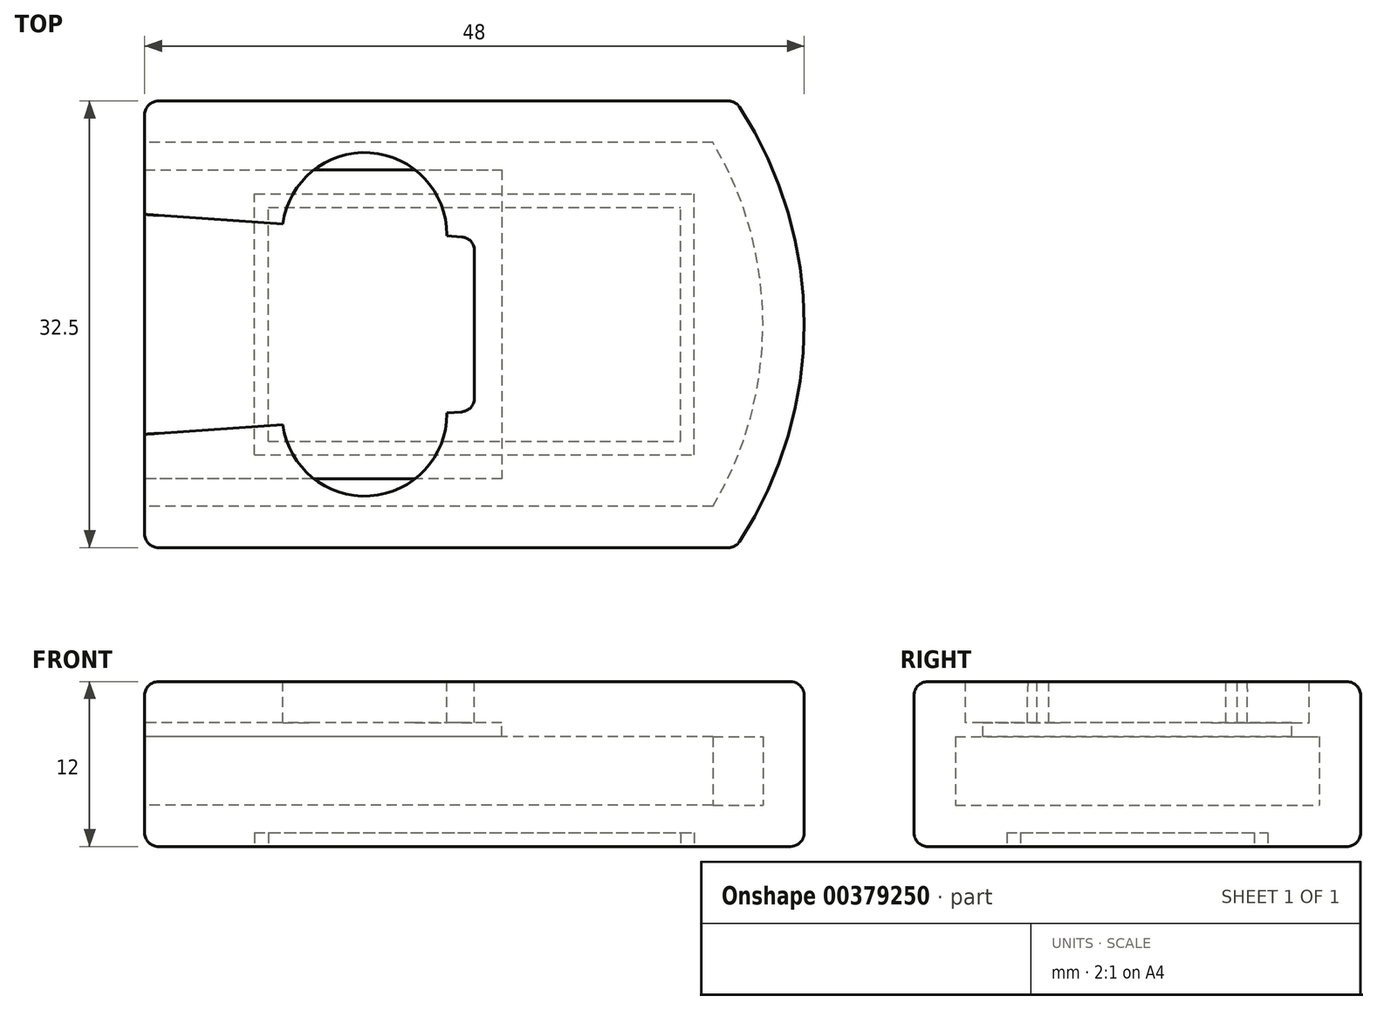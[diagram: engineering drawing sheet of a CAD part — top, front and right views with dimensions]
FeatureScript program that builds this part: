
annotation { "Feature Type Name" : "Feature", "Feature Type Description" : "" }
export const myFeature = defineFeature(function(context is Context, id is Id, definition is map)
    precondition{}
    {
        {
            var Q0;
            Q0=qCreatedBy(makeId("Top.planeOp"),FACE);
            var sketch = newSketch(context, id + "F0", { "sketchPlane" : qUnion([Q0])});
            skLineSegment(sketch, "E0.bottom", {"start": v(24, -16.25) * mm, "end": v(-24, -16.25) * mm});
            skLineSegment(sketch, "E0.top", {"start": v(24, 16.25) * mm, "end": v(-24, 16.25) * mm});
            skLineSegment(sketch, "E0.left", {"start": v(24, -16.25) * mm, "end": v(24, 16.25) * mm});
            skLineSegment(sketch, "E0.right", {"start": v(-24, -16.25) * mm, "end": v(-24, 16.25) * mm});
            skPoint(sketch, "E0.middle", {"position": v(0, 0) * mm});
            skArc(sketch, "E1", {"start": v(19, -16.25) * mm, "mid": v(24, 0) * mm, "end": v(19, 16.25) * mm});
            skSolve(sketch);
        }
        {
            var Q0;
            {var subQ4=sQuery(id+"F0.wireOp",EDGE,"E0.right");Q0=makeQuery(id+"F0.imprint","IMPRINT",FACE,{"disambiguationData":[TD([[makeQuery(id+"F0.imprint","IMPRINT",EDGE,{"derivedFrom":subQ4}),-1.0]])]});}
            extrude(context, id + "F1", {"entities" : qUnion([Q0]), "depth" : 12 * mm});
        }
        {
            var Q0;
            Q0=makeQuery(id+"F1.opExtrude","SWEPT_FACE",FACE,{"disambiguationData":[OSD([sQuery(id+"F0.wireOp",EDGE,"E0.right")])]});
            shell(context, id + "F2", {"entities" : qUnion([Q0]), "thickness" : 3 * mm});
        }
        {
            var Q0;
            Q0=makeQuery(id+"F1.opExtrude","CAP_FACE",FACE,{"disambiguationData":[OSD([sQuery(id+"F0.wireOp",EDGE,"E0.bottom"),sQuery(id+"F0.wireOp",EDGE,"E0.top"),sQuery(id+"F0.wireOp",EDGE,"E0.right"),sQuery(id+"F0.wireOp",EDGE,"FjGHQm9p-3ohD-EudD-jZ4d-5vYzKEwLbSdo")])],"isStart":false});
            var sketch = newSketch(context, id + "F3", { "sketchPlane" : qUnion([Q0])});
            skLineSegment(sketch, "E2.0.0", {"start": v(-24, -16.25) * mm, "end": v(-24, -16.25) * mm});
            skLineSegment(sketch, "E2.0.2", {"start": v(24, 16.25) * mm, "end": v(-24, 16.25) * mm});
            skLineSegment(sketch, "E2.0.3", {"start": v(-24, 16.25) * mm, "end": v(-24, -16.25) * mm});
            skLineSegment(sketch, "E3.bottom", {"start": v(-8, 12.5) * mm, "end": v(-8, 12.5) * mm});
            skLineSegment(sketch, "E3.top", {"start": v(-8, -12.5) * mm, "end": v(-8, -12.5) * mm});
            skLineSegment(sketch, "E3.left", {"start": v(-14, 6.5) * mm, "end": v(-14, -6.5) * mm});
            skLineSegment(sketch, "E3.right", {"start": v(-2, 6.5) * mm, "end": v(-2, -6.5) * mm});
            skPoint(sketch, "E3.middle", {"position": v(-8, 0) * mm});
            skLineSegment(sketch, "E4", {"start": v(-24, 0) * mm, "end": v(24, 0) * mm, "construction": true});
            skPoint(sketch, "E5.visualSharp", {"position": v(-14, 12.5) * mm});
            skArc(sketch, "E5.filletArc", {"start": v(-8, 12.5) * mm, "mid": v(-12.24, 10.74) * mm, "end": v(-14, 6.5) * mm});
            skPoint(sketch, "E6.visualSharp", {"position": v(-2, 12.5) * mm});
            skArc(sketch, "E6.filletArc", {"start": v(-2, 6.5) * mm, "mid": v(-3.76, 10.74) * mm, "end": v(-8, 12.5) * mm});
            skPoint(sketch, "E7.visualSharp", {"position": v(-2, -12.5) * mm});
            skArc(sketch, "E7.filletArc", {"start": v(-8, -12.5) * mm, "mid": v(-3.76, -10.74) * mm, "end": v(-2, -6.5) * mm});
            skPoint(sketch, "E8.visualSharp", {"position": v(-14, -12.5) * mm});
            skArc(sketch, "E8.filletArc", {"start": v(-14, -6.5) * mm, "mid": v(-12.24, -10.74) * mm, "end": v(-8, -12.5) * mm});
            skLineSegment(sketch, "E9", {"start": v(-24, 8) * mm, "end": v(0, 6.3) * mm});
            skLineSegment(sketch, "E10", {"start": v(0, 6.3) * mm, "end": v(0, 0) * mm});
            skLineSegment(sketch, "E11.MirrorCS", {"start": v(-24, -8) * mm, "end": v(0, -6.3) * mm});
            skLineSegment(sketch, "E12.MirrorCS", {"start": v(0, -6.3) * mm, "end": v(0, 0) * mm});
            skSolve(sketch);
        }
        {
            var Q0;
            {var subQ0=sQuery(id+"F3.wireOp",EDGE,"E5.filletArc");Q0=makeQuery(id+"F3.imprint","IMPRINT",FACE,{"disambiguationData":[TD([[makeQuery(id+"F3.imprint","IMPRINT",EDGE,{"derivedFrom":subQ0}),1.0]])]});}
            var Q1;
            {var subQ0=sQuery(id+"F3.wireOp",EDGE,"E7.filletArc");Q1=makeQuery(id+"F3.imprint","IMPRINT",FACE,{"disambiguationData":[TD([[makeQuery(id+"F3.imprint","IMPRINT",EDGE,{"derivedFrom":subQ0}),1.0]])]});}
            var Q2;
            {var subQ1=sQuery(id+"F3.wireOp",EDGE,"E3.left");Q2=makeQuery(id+"F3.imprint","IMPRINT",FACE,{"disambiguationData":[TD([[makeQuery(id+"F3.imprint","IMPRINT",EDGE,{"derivedFrom":subQ1}),1.0]])]});}
            var Q3;
            {var subQ1=sQuery(id+"F3.wireOp",EDGE,"E3.left");Q3=makeQuery(id+"F3.imprint","IMPRINT",FACE,{"disambiguationData":[TD([[makeQuery(id+"F3.imprint","IMPRINT",EDGE,{"derivedFrom":subQ1}),-1.0]])]});}
            var Q4;
            {var subQ4=sQuery(id+"F3.wireOp",EDGE,"E10");Q4=makeQuery(id+"F3.imprint","IMPRINT",FACE,{"disambiguationData":[TD([[makeQuery(id+"F3.imprint","IMPRINT",EDGE,{"derivedFrom":subQ4}),-1.0]])]});}
            var Q5;
            {var subQ0=sQuery(id+"F0.wireOp",EDGE,"FjGHQm9p-3ohD-EudD-jZ4d-5vYzKEwLbSdo");var subQ1=sQuery(id+"F0.wireOp",EDGE,"E0.right");var subQ2=sQuery(id+"F0.wireOp",EDGE,"E0.top");var subQ3=sQuery(id+"F0.wireOp",EDGE,"E0.bottom");Q5=makeQuery(id+"F2.opShell","OFFSET_FACE",FACE,{"disambiguationData":[OSD([subQ3,subQ2,subQ1,subQ0]),TDD([makeQuery(id+"F1.opExtrude","CAP_FACE",FACE,{"disambiguationData":[OSD([subQ3,subQ2,subQ1,subQ0])],"isStart":false})])]});}
            extrude(context, id + "F4", {"entities" : qUnion([Q0, Q1, Q2, Q3, Q4]), "operationType" : NewBodyOperationType.REMOVE, "endBound" : BoundingType.UP_TO_SURFACE, "oppositeDirection" : true, "endBoundEntityFace" : qUnion([Q5]), "depth" : 25 * mm});
        }
        {
            var Q0;
            Q0=makeQuery(id+"F4.boolean.opBoolean","COPY",EDGE,{"derivedFrom":makeQuery(id+"F4.opExtrude","SWEPT_EDGE",EDGE,{"disambiguationData":[OSD([sQuery(id+"F3.wireOp",EDGE,"E9"),sQuery(id+"F3.wireOp",EDGE,"E10")])]})});
            var Q1;
            Q1=makeQuery(id+"F4.boolean.opBoolean","COPY",EDGE,{"derivedFrom":makeQuery(id+"F4.opExtrude","SWEPT_EDGE",EDGE,{"disambiguationData":[OSD([sQuery(id+"F3.wireOp",EDGE,"E11.MirrorCS"),sQuery(id+"F3.wireOp",EDGE,"E12.MirrorCS")])]})});
            fillet(context, id + "F5", {"entities" : qUnion([Q0, Q1]), "radius" : 1 * mm, "tangentPropagation" : true, "allowEdgeOverflow" : false});
        }
        {
            var Q0;
            Q0=makeQuery(id+"F1.opExtrude","CAP_FACE",FACE,{"disambiguationData":[OSD([sQuery(id+"F0.wireOp",EDGE,"E0.bottom"),sQuery(id+"F0.wireOp",EDGE,"E0.top"),sQuery(id+"F0.wireOp",EDGE,"E0.right"),sQuery(id+"F0.wireOp",EDGE,"E1")])],"isStart":true});
            var sketch = newSketch(context, id + "F6", { "sketchPlane" : qUnion([Q0])});
            skLineSegment(sketch, "E13.bottom", {"start": v(-16, 9.5) * mm, "end": v(16, 9.5) * mm});
            skLineSegment(sketch, "E13.top", {"start": v(-16, -9.5) * mm, "end": v(16, -9.5) * mm});
            skLineSegment(sketch, "E13.left", {"start": v(-16, 9.5) * mm, "end": v(-16, -9.5) * mm});
            skLineSegment(sketch, "E13.right", {"start": v(16, 9.5) * mm, "end": v(16, -9.5) * mm});
            skPoint(sketch, "E13.middle", {"position": v(0, 0) * mm});
            skLineSegment(sketch, "E14.0", {"start": v(-15, -8.5) * mm, "end": v(15, -8.5) * mm});
            skLineSegment(sketch, "E14.1", {"start": v(-15, 8.5) * mm, "end": v(-15, -8.5) * mm});
            skLineSegment(sketch, "E14.2", {"start": v(-15, 8.5) * mm, "end": v(15, 8.5) * mm});
            skLineSegment(sketch, "E14.3", {"start": v(15, 8.5) * mm, "end": v(15, -8.5) * mm});
            skSolve(sketch);
        }
        {
            var Q0;
            Q0=makeQuery(id+"F6.imprint","IMPRINT",FACE,{"disambiguationData":[TD([[makeQuery(id+"F6.imprint","IMPRINT",EDGE,{"derivedFrom":sQuery(id+"F6.wireOp",EDGE,"E13.bottom")}),-1.0]])]});
            extrude(context, id + "F7", {"entities" : qUnion([Q0]), "operationType" : NewBodyOperationType.REMOVE, "oppositeDirection" : true, "depth" : 1 * mm});
        }
        {
            var Q0;
            {var subQ0=sQuery(id+"F0.wireOp",EDGE,"E1");var subQ1=sQuery(id+"F0.wireOp",EDGE,"E0.right");var subQ2=sQuery(id+"F0.wireOp",EDGE,"E0.top");var subQ3=sQuery(id+"F0.wireOp",EDGE,"E0.bottom");Q0=makeQuery(id+"F2.opShell","OFFSET_FACE",FACE,{"disambiguationData":[OSD([subQ3,subQ2,subQ1,subQ0]),TDD([makeQuery(id+"F1.opExtrude","CAP_FACE",FACE,{"disambiguationData":[OSD([subQ3,subQ2,subQ1,subQ0])],"isStart":false})])]});}
            var sketch = newSketch(context, id + "F8", { "sketchPlane" : qUnion([Q0])});
            skLineSegment(sketch, "E15.0.12", {"start": v(-24, -13.25) * mm, "end": v(17.36, -13.25) * mm});
            skArc(sketch, "E15.0.13", {"start": v(17.36, -13.25) * mm, "mid": v(21, 0) * mm, "end": v(17.36, 13.25) * mm});
            skLineSegment(sketch, "E15.0.14", {"start": v(17.36, 13.25) * mm, "end": v(-24, 13.25) * mm});
            skLineSegment(sketch, "E15.0.15", {"start": v(-24, 13.25) * mm, "end": v(-24, 11.25) * mm});
            skLineSegment(sketch, "E16.0", {"start": v(2, -11.25) * mm, "end": v(2, 11.25) * mm});
            skLineSegment(sketch, "E17.0", {"start": v(-24, -11.25) * mm, "end": v(2, -11.25) * mm});
            skLineSegment(sketch, "E18.0", {"start": v(2, 11.25) * mm, "end": v(-24, 11.25) * mm});
            skPoint(sketch, "E19.orphan", {"position": v(-24, 8) * mm});
            skPoint(sketch, "E20.orphan", {"position": v(-24, -8) * mm});
            skLineSegment(sketch, "E21", {"start": v(-24, -13.25) * mm, "end": v(-24, -11.25) * mm});
            skSolve(sketch);
        }
        {
            var Q0;
            {var subQ0=sQuery(id+"F8.wireOp",EDGE,"E18.0");var subQ1=sQuery(id+"F3.wireOp",EDGE,"E8.filletArc");var subQ2=sQuery(id+"F3.wireOp",EDGE,"E7.filletArc");var subQ3=sQuery(id+"F0.wireOp",EDGE,"E1");var subQ4=sQuery(id+"F0.wireOp",EDGE,"E0.right");var subQ5=sQuery(id+"F0.wireOp",EDGE,"E0.top");var subQ6=sQuery(id+"F0.wireOp",EDGE,"E0.bottom");var subQ7=makeQuery(id+"F4.boolean.opBoolean","COPY",EDGE,{"derivedFrom":makeQuery(id+"F4.opExtrude","TWEAK_EDGE",EDGE,{"derivedFrom":[makeQuery(id+"F2.opShell","OFFSET_FACE",FACE,{"disambiguationData":[OSD([subQ6,subQ5,subQ4,subQ3]),TDD([makeQuery(id+"F1.opExtrude","CAP_FACE",FACE,{"disambiguationData":[OSD([subQ6,subQ5,subQ4,subQ3])],"isStart":false})])]}),makeQuery(id+"F3.imprint","IMPRINT",EDGE,{"derivedFrom":subQ2}),makeQuery(id+"F3.imprint","IMPRINT",EDGE,{"disambiguationData":[TD([[makeQuery(id+"F3.imprint","INTERSECT",VERTEX,{"derivedFrom":[subQ2,subQ1]}),1.0]])],"derivedFrom":subQ1})]})});var subQ8=makeQuery(id+"F8.imprint","INTERSECT",VERTEX,{"disambiguationData":[OD(0.0)],"derivedFrom":[subQ7,subQ0]});Q0=makeQuery(id+"F8.imprint","IMPRINT",FACE,{"disambiguationData":[TD([[makeQuery(id+"F8.imprint","IMPRINT",EDGE,{"disambiguationData":[TD([[subQ8,-1.0]])],"derivedFrom":subQ0}),-1.0]])]});}
            var Q1;
            {var subQ0=sQuery(id+"F8.wireOp",EDGE,"E17.0");var subQ1=sQuery(id+"F3.wireOp",EDGE,"E6.filletArc");var subQ2=sQuery(id+"F3.wireOp",EDGE,"E5.filletArc");var subQ3=sQuery(id+"F0.wireOp",EDGE,"E1");var subQ4=sQuery(id+"F0.wireOp",EDGE,"E0.right");var subQ5=sQuery(id+"F0.wireOp",EDGE,"E0.top");var subQ6=sQuery(id+"F0.wireOp",EDGE,"E0.bottom");var subQ7=makeQuery(id+"F4.boolean.opBoolean","COPY",EDGE,{"derivedFrom":makeQuery(id+"F4.opExtrude","TWEAK_EDGE",EDGE,{"derivedFrom":[makeQuery(id+"F2.opShell","OFFSET_FACE",FACE,{"disambiguationData":[OSD([subQ6,subQ5,subQ4,subQ3]),TDD([makeQuery(id+"F1.opExtrude","CAP_FACE",FACE,{"disambiguationData":[OSD([subQ6,subQ5,subQ4,subQ3])],"isStart":false})])]}),makeQuery(id+"F3.imprint","IMPRINT",EDGE,{"disambiguationData":[TD([[makeQuery(id+"F3.imprint","INTERSECT",VERTEX,{"derivedFrom":[subQ2,subQ1]}),-1.0]])],"derivedFrom":subQ2}),makeQuery(id+"F3.imprint","IMPRINT",EDGE,{"derivedFrom":subQ1})]})});var subQ8=makeQuery(id+"F8.imprint","INTERSECT",VERTEX,{"disambiguationData":[OD(0.0)],"derivedFrom":[subQ7,subQ0]});Q1=makeQuery(id+"F8.imprint","IMPRINT",FACE,{"disambiguationData":[TD([[makeQuery(id+"F8.imprint","IMPRINT",EDGE,{"disambiguationData":[TD([[subQ8,-1.0]])],"derivedFrom":subQ0}),-1.0]])]});}
            var Q2;
            Q2=makeQuery(id+"F8.imprint","IMPRINT",FACE,{"disambiguationData":[TD([[makeQuery(id+"F8.imprint","IMPRINT",EDGE,{"derivedFrom":sQuery(id+"F8.wireOp",EDGE,"E15.0.13")}),-1.0]])]});
            extrude(context, id + "F9", {"entities" : qUnion([Q0, Q1, Q2]), "operationType" : NewBodyOperationType.ADD, "depth" : 1 * mm});
        }
        {
            var Q0;
            Q0=makeQuery(id+"F1.opExtrude","CAP_EDGE",EDGE,{"disambiguationData":[OSD([sQuery(id+"F0.wireOp",EDGE,"E0.bottom")])],"isStart":false});
            var Q1;
            Q1=makeQuery(id+"F1.opExtrude","CAP_EDGE",EDGE,{"disambiguationData":[OSD([sQuery(id+"F0.wireOp",EDGE,"E1")])],"isStart":false});
            var Q2;
            Q2=makeQuery(id+"F1.opExtrude","CAP_EDGE",EDGE,{"disambiguationData":[OSD([sQuery(id+"F0.wireOp",EDGE,"E0.top")])],"isStart":false});
            var Q3;
            Q3=makeQuery(id+"F1.opExtrude","SWEPT_EDGE",EDGE,{"disambiguationData":[OSD([sQuery(id+"F0.wireOp",EDGE,"E0.bottom"),sQuery(id+"F0.wireOp",EDGE,"E1")])]});
            var Q4;
            Q4=makeQuery(id+"F1.opExtrude","SWEPT_EDGE",EDGE,{"disambiguationData":[OSD([sQuery(id+"F0.wireOp",EDGE,"E0.top"),sQuery(id+"F0.wireOp",EDGE,"E1")])]});
            var Q5;
            Q5=makeQuery(id+"F1.opExtrude","CAP_EDGE",EDGE,{"disambiguationData":[OSD([sQuery(id+"F0.wireOp",EDGE,"E1")])],"isStart":true});
            var Q6;
            Q6=makeQuery(id+"F1.opExtrude","CAP_EDGE",EDGE,{"disambiguationData":[OSD([sQuery(id+"F0.wireOp",EDGE,"E0.top")])],"isStart":true});
            var Q7;
            Q7=makeQuery(id+"F1.opExtrude","CAP_EDGE",EDGE,{"disambiguationData":[OSD([sQuery(id+"F0.wireOp",EDGE,"E0.bottom")])],"isStart":true});
            var Q8;
            Q8=makeQuery(id+"F1.opExtrude","SWEPT_EDGE",EDGE,{"disambiguationData":[OSD([sQuery(id+"F0.wireOp",EDGE,"E0.bottom"),sQuery(id+"F0.wireOp",EDGE,"E0.right")])]});
            var Q9;
            {var subQ0=sQuery(id+"F0.wireOp",EDGE,"E0.bottom");var subQ1=sQuery(id+"F0.wireOp",EDGE,"E0.right");Q9=makeQuery(id+"F4.boolean.opBoolean","SPLIT",EDGE,{"disambiguationData":[TD([makeQuery(id+"F1.opExtrude","SWEPT_FACE",FACE,{"disambiguationData":[OSD([subQ0])]})])],"derivedFrom":makeQuery(id+"F1.opExtrude","CAP_EDGE",EDGE,{"disambiguationData":[OSD([subQ1])],"isStart":false})});}
            var Q10;
            Q10=makeQuery(id+"F1.opExtrude","CAP_EDGE",EDGE,{"disambiguationData":[OSD([sQuery(id+"F0.wireOp",EDGE,"E0.right")])],"isStart":true});
            var Q11;
            {var subQ0=sQuery(id+"F0.wireOp",EDGE,"E0.right");var subQ1=sQuery(id+"F0.wireOp",EDGE,"E0.top");Q11=makeQuery(id+"F4.boolean.opBoolean","SPLIT",EDGE,{"disambiguationData":[TD([makeQuery(id+"F1.opExtrude","SWEPT_FACE",FACE,{"disambiguationData":[OSD([subQ1])]})])],"derivedFrom":makeQuery(id+"F1.opExtrude","CAP_EDGE",EDGE,{"disambiguationData":[OSD([subQ0])],"isStart":false})});}
            var Q12;
            Q12=makeQuery(id+"F1.opExtrude","SWEPT_EDGE",EDGE,{"disambiguationData":[OSD([sQuery(id+"F0.wireOp",EDGE,"E0.top"),sQuery(id+"F0.wireOp",EDGE,"E0.right")])]});
            fillet(context, id + "F10", {"entities" : qUnion([Q0, Q1, Q2, Q3, Q4, Q5, Q6, Q7, Q8, Q9, Q10, Q11, Q12]), "radius" : 1 * mm, "tangentPropagation" : true, "allowEdgeOverflow" : false});
        }
    });
